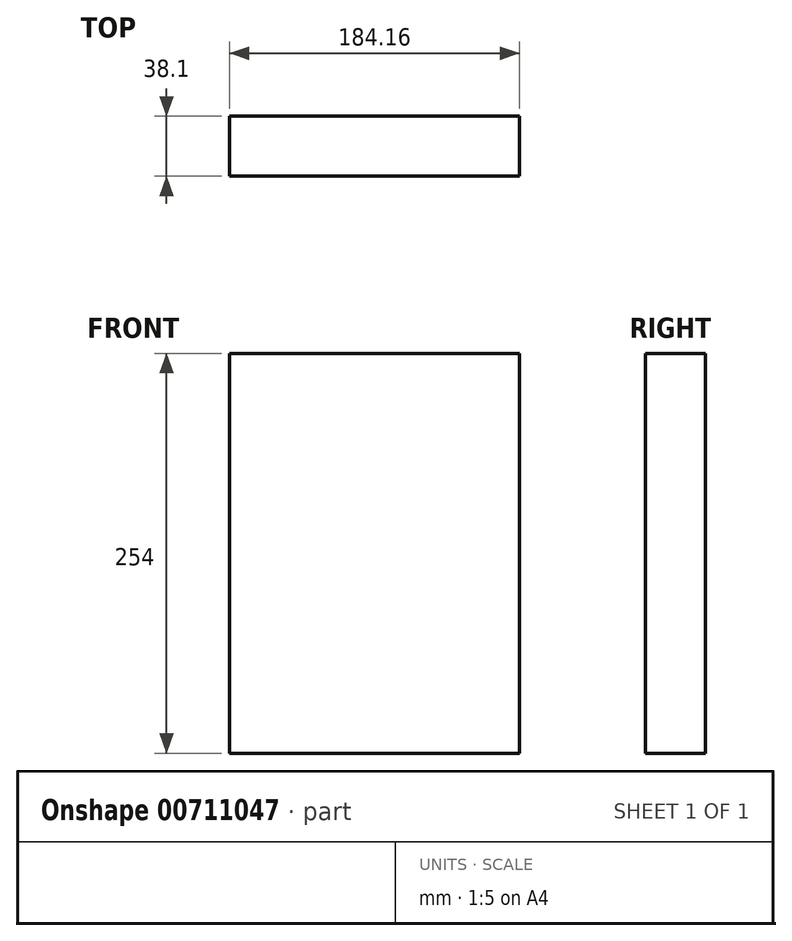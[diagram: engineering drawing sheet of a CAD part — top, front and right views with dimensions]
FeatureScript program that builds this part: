
annotation { "Feature Type Name" : "Feature", "Feature Type Description" : "" }
export const myFeature = defineFeature(function(context is Context, id is Id, definition is map)
    precondition{}
    {
        {
            var Q0;
            Q0=qCreatedBy(makeId("Top.planeOp"),FACE);
            var sketch = newSketch(context, id + "F0", { "sketchPlane" : qUnion([Q0])});
            skLineSegment(sketch, "E0.bottom", {"start": v(92.08, 19.05) * mm, "end": v(-92.08, 19.05) * mm});
            skLineSegment(sketch, "E0.top", {"start": v(92.08, -19.05) * mm, "end": v(-92.07, -19.05) * mm});
            skLineSegment(sketch, "E0.left", {"start": v(92.08, 19.05) * mm, "end": v(92.08, -19.05) * mm});
            skLineSegment(sketch, "E0.right", {"start": v(-92.08, 19.05) * mm, "end": v(-92.08, -19.05) * mm});
            skPoint(sketch, "E0.middle", {"position": v(0, 0) * mm});
            skSolve(sketch);
        }
        {
            var Q0;
            Q0=makeQuery(id+"F0.imprint","IMPRINT",FACE,{"disambiguationData":[TD([[makeQuery(id+"F0.imprint","IMPRINT",EDGE,{"derivedFrom":sQuery(id+"F0.wireOp",EDGE,"E0.bottom")}),1.0]])]});
            extrude(context, id + "F1", {"entities" : qUnion([Q0]), "depth" : 254 * mm, "offsetDistance" : 25.4 * mm});
        }
    });
